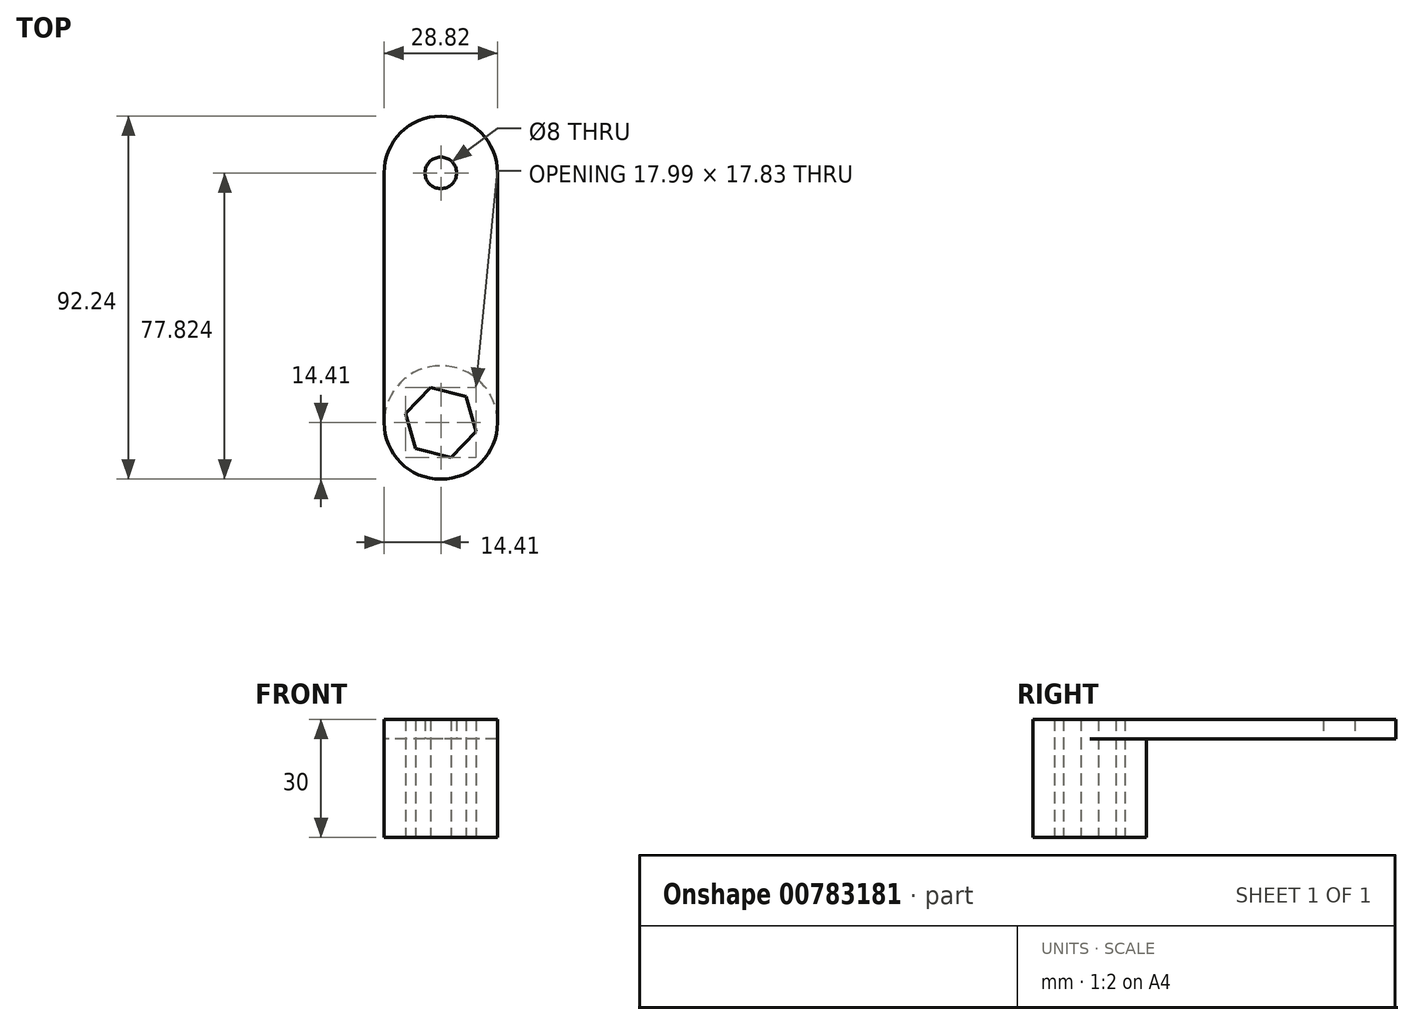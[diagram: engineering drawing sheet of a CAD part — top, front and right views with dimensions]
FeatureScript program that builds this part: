
annotation { "Feature Type Name" : "Feature", "Feature Type Description" : "" }
export const myFeature = defineFeature(function(context is Context, id is Id, definition is map)
    precondition{}
    {
        {
            var Q0;
            Q0=qCreatedBy(makeId("Top.planeOp"),FACE);
            var sketch = newSketch(context, id + "F0", { "sketchPlane" : qUnion([Q0])});
            skCircle(sketch, "E0", {"center": v(0, 0) * mm, "radius": 14.41 * mm});
            skCircle(sketch, "E1.cCircle", {"center": v(0, 0) * mm, "radius": 8.03 * mm, "construction": true});
            skLineSegment(sketch, "E1.0", {"start": v(9, -2.26) * mm, "end": v(2.54, -8.92) * mm});
            skLineSegment(sketch, "E1.1", {"start": v(2.54, -8.92) * mm, "end": v(-6.45, -6.66) * mm});
            skLineSegment(sketch, "E1.2", {"start": v(-6.45, -6.66) * mm, "end": v(-9, 2.26) * mm});
            skLineSegment(sketch, "E1.3", {"start": v(-9, 2.26) * mm, "end": v(-2.54, 8.92) * mm});
            skLineSegment(sketch, "E1.4", {"start": v(-2.54, 8.92) * mm, "end": v(6.45, 6.66) * mm});
            skLineSegment(sketch, "E1.5", {"start": v(6.45, 6.66) * mm, "end": v(9, -2.26) * mm});
            skPoint(sketch, "E1.0.midPoint", {"position": v(5.77, -5.59) * mm});
            skSolve(sketch);
        }
        {
            var Q0;
            Q0 = qSketchRegion(id + "F0", true);
            extrude(context, id + "F1", {"entities" : qUnion([Q0]), "depth" : 25 * mm, "offsetDistance" : 25 * mm});
        }
        {
            var Q0;
            Q0=makeQuery(id+"F1.opExtrude","CAP_FACE",FACE,{"disambiguationData":[OSD([sQuery(id+"F0.wireOp",EDGE,"E0"),sQuery(id+"F0.wireOp",EDGE,"E1.0"),sQuery(id+"F0.wireOp",EDGE,"E1.1"),sQuery(id+"F0.wireOp",EDGE,"E1.2"),sQuery(id+"F0.wireOp",EDGE,"E1.3"),sQuery(id+"F0.wireOp",EDGE,"E1.4"),sQuery(id+"F0.wireOp",EDGE,"E1.5")])],"isStart":false});
            var sketch = newSketch(context, id + "F2", { "sketchPlane" : qUnion([Q0])});
            skLineSegment(sketch, "E2", {"start": v(-14.41, 0) * mm, "end": v(-14.41, 63.41) * mm});
            skLineSegment(sketch, "E3", {"start": v(-14.41, 63.41) * mm, "end": v(14.41, 63.41) * mm});
            skLineSegment(sketch, "E4", {"start": v(14.41, 63.41) * mm, "end": v(14.41, 0) * mm});
            skArc(sketch, "E5", {"start": v(14.41, 63.41) * mm, "mid": v(0, 77.83) * mm, "end": v(-14.41, 63.41) * mm});
            skCircle(sketch, "E6", {"center": v(0, 63.41) * mm, "radius": 4 * mm});
            skSolve(sketch);
        }
        {
            var Q0;
            {var subQ1=sQuery(id+"F2.wireOp",EDGE,"E2");Q0=makeQuery(id+"F2.imprint","IMPRINT",FACE,{"disambiguationData":[TD([[makeQuery(id+"F2.imprint","IMPRINT",EDGE,{"derivedFrom":subQ1}),-1.0]])]});}
            var Q1;
            Q1=makeQuery(id+"F2.imprint","IMPRINT",FACE,{"disambiguationData":[TD([[makeQuery(id+"F2.imprint","IMPRINT",EDGE,{"derivedFrom":makeQuery(id+"F1.opExtrude","CAP_EDGE",EDGE,{"disambiguationData":[OSD([sQuery(id+"F0.wireOp",EDGE,"E1.0")])],"isStart":false})}),1.0]])]});
            var Q2;
            {var subQ0=sQuery(id+"F2.wireOp",EDGE,"E5");Q2=makeQuery(id+"F2.imprint","IMPRINT",FACE,{"disambiguationData":[TD([[makeQuery(id+"F2.imprint","IMPRINT",EDGE,{"derivedFrom":subQ0}),1.0]])]});}
            extrude(context, id + "F3", {"entities" : qUnion([Q0, Q1, Q2]), "operationType" : NewBodyOperationType.ADD, "depth" : 5 * mm, "offsetDistance" : 25 * mm});
        }
    });
